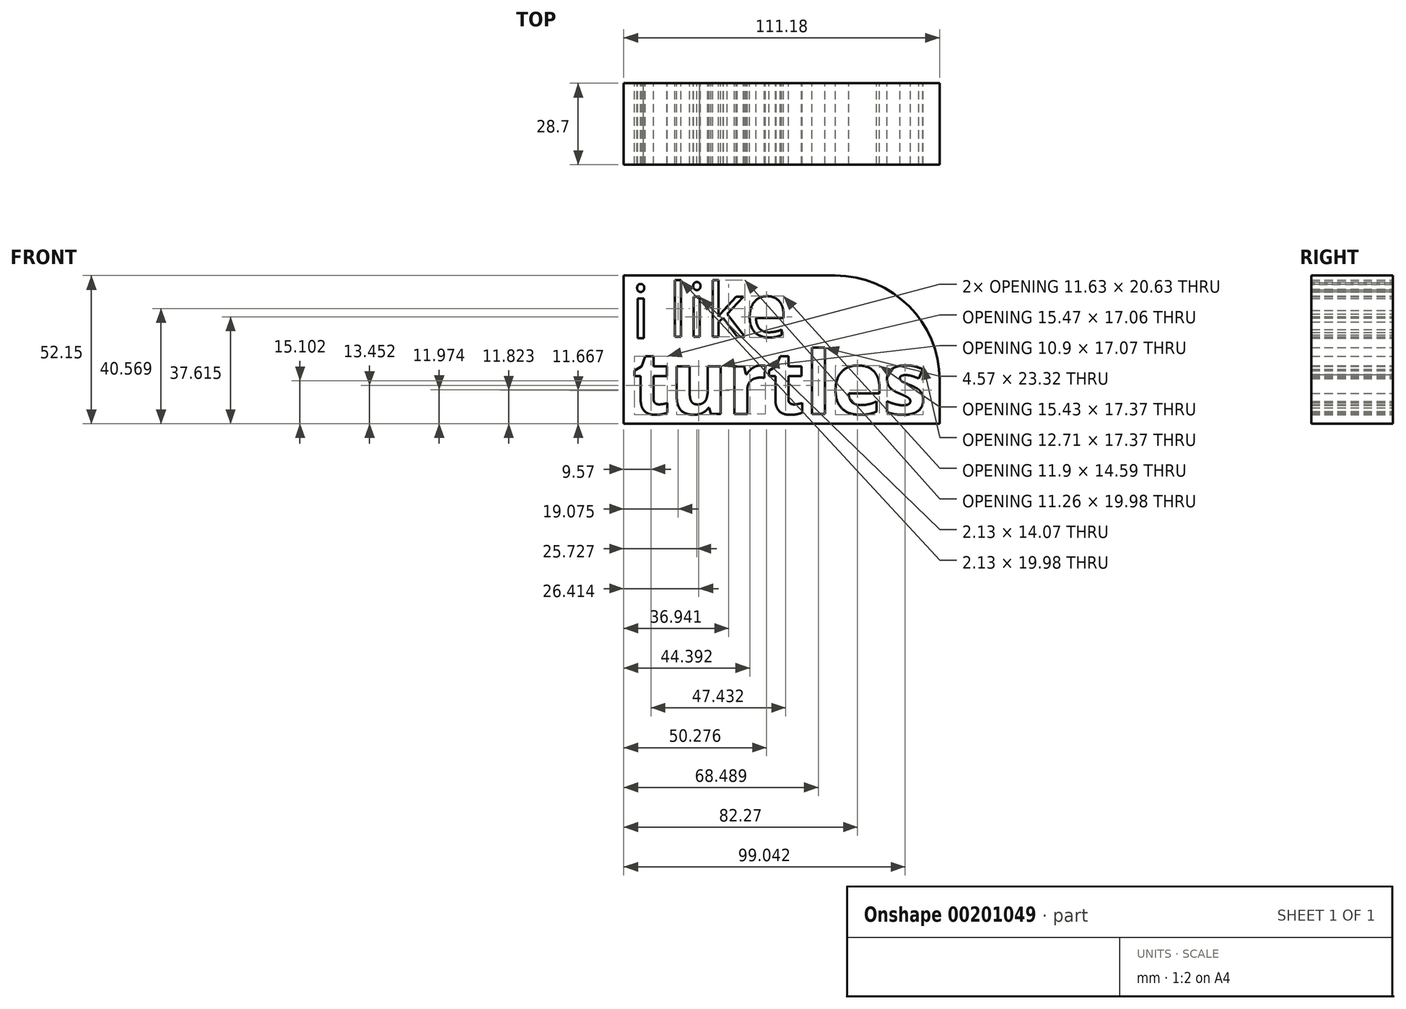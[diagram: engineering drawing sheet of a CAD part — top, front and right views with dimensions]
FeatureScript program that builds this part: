
annotation { "Feature Type Name" : "Feature", "Feature Type Description" : "" }
export const myFeature = defineFeature(function(context is Context, id is Id, definition is map)
    precondition{}
    {
        {
            var Q0;
            Q0=qCreatedBy(makeId("Front.planeOp"),FACE);
            var sketch = newSketch(context, id + "F0", { "sketchPlane" : qUnion([Q0])});
            skText(sketch, "E0", { "text": "i ", "fontName": "OpenSans-Regular.ttf"});
            skText(sketch, "E1", { "text": "like", "fontName": "OpenSans-Regular.ttf"});
            skText(sketch, "E2", { "text": "turtles", "fontName": "OpenSans-Bold.ttf"});
            skLineSegment(sketch, "E3.bottom", {"start": v(-43.68, -62.54) * mm, "end": v(67.5, -62.54) * mm});
            skLineSegment(sketch, "E3.top", {"start": v(-43.68, -10.4) * mm, "end": v(30.7, -10.4) * mm});
            skLineSegment(sketch, "E3.left", {"start": v(-43.68, -62.54) * mm, "end": v(-43.68, -10.4) * mm});
            skLineSegment(sketch, "E3.right", {"start": v(67.5, -62.54) * mm, "end": v(67.5, -47.18) * mm});
            skPoint(sketch, "E4.visualSharp", {"position": v(67.5, -10.4) * mm});
            skArc(sketch, "E4.filletArc", {"start": v(67.5, -47.18) * mm, "mid": v(56.73, -21.17) * mm, "end": v(30.7, -10.4) * mm});
            const initialGuessF0  = {"E0": [-0.04103, -0.0325, 1, 0, 0.0188], "E1": [-0.02793, -0.03196, 1, 0, 0.01893], "E2": [-0.04063, -0.0591, 1, 0, 0.0221]};
            skSetInitialGuess(sketch, initialGuessF0);
            skSolve(sketch);
        }
        {
            var Q0;
            Q0 = qSketchRegion(id + "F0", true);
            extrude(context, id + "F1", {"entities" : qUnion([Q0]), "depth" : 28.7 * mm});
        }
    });
